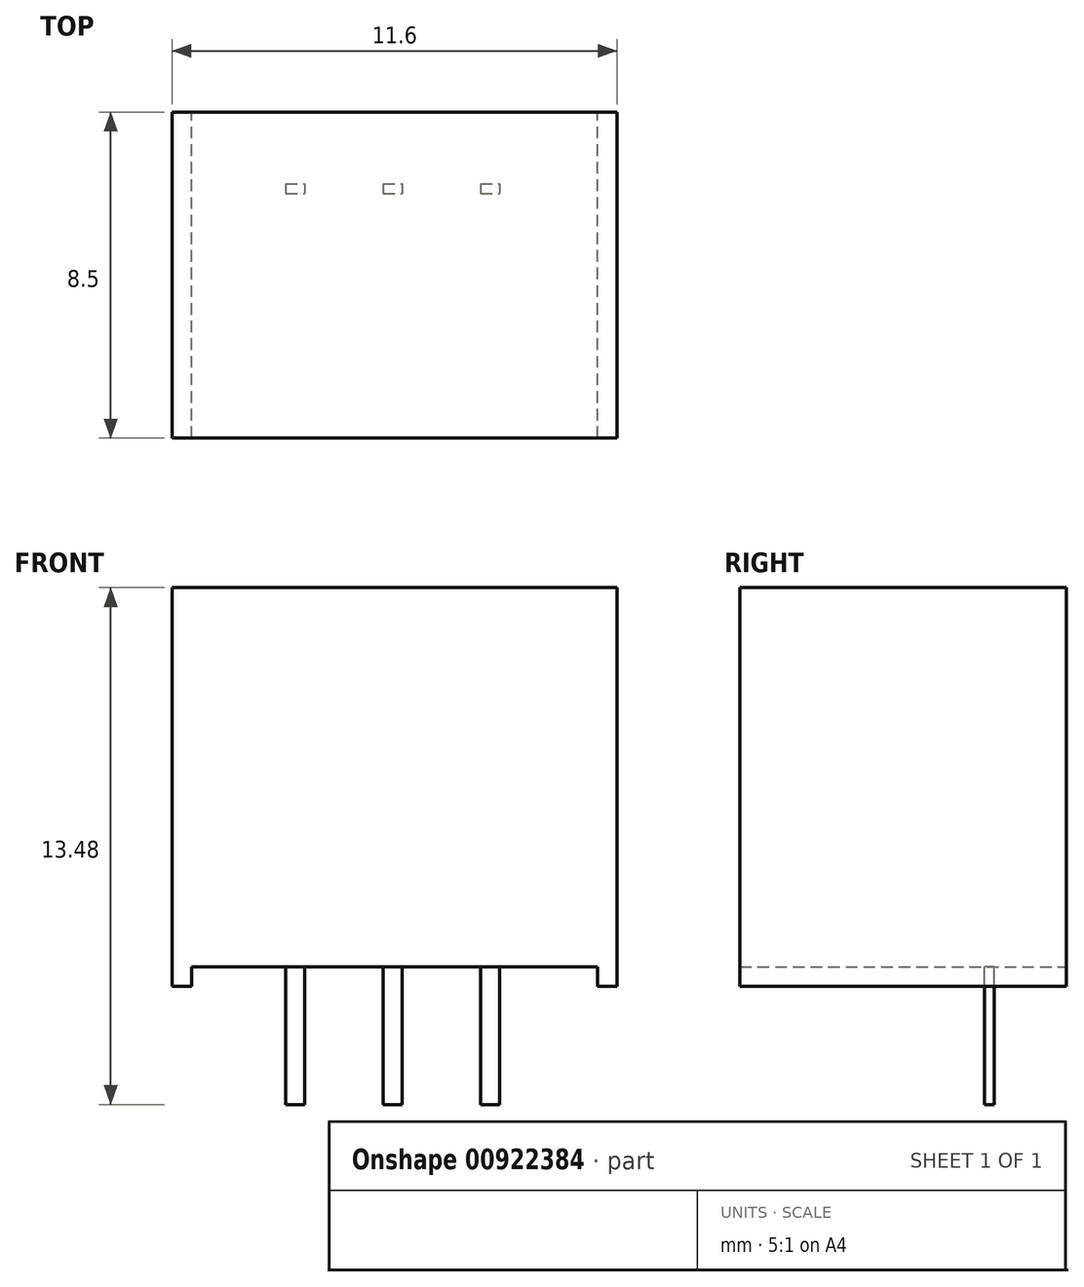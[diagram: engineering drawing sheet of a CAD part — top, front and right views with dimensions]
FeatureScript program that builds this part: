
annotation { "Feature Type Name" : "Feature", "Feature Type Description" : "" }
export const myFeature = defineFeature(function(context is Context, id is Id, definition is map)
    precondition{}
    {
        {
            var Q0;
            Q0=qCreatedBy(makeId("Front.planeOp"),FACE);
            var sketch = newSketch(context, id + "F0", { "sketchPlane" : qUnion([Q0])});
            skLineSegment(sketch, "E0.bottom", {"start": v(-5.8, 5.2) * mm, "end": v(5.8, 5.2) * mm});
            skLineSegment(sketch, "E0.top", {"start": v(-5.8, -5.2) * mm, "end": v(5.8, -5.2) * mm});
            skLineSegment(sketch, "E0.left", {"start": v(-5.8, 5.2) * mm, "end": v(-5.8, -5.2) * mm});
            skLineSegment(sketch, "E0.right", {"start": v(5.8, 5.2) * mm, "end": v(5.8, -5.2) * mm});
            skPoint(sketch, "E0.middle", {"position": v(0, 0) * mm});
            skLineSegment(sketch, "E1", {"start": v(-5.8, -5.2) * mm, "end": v(-5.29, -5.2) * mm});
            skLineSegment(sketch, "E2", {"start": v(-5.29, -5.2) * mm, "end": v(-5.29, -4.69) * mm});
            skLineSegment(sketch, "E3.MirrorCS", {"start": v(5.8, -5.2) * mm, "end": v(5.29, -5.2) * mm});
            skLineSegment(sketch, "E4.MirrorCS", {"start": v(5.29, -5.2) * mm, "end": v(5.29, -4.69) * mm});
            skLineSegment(sketch, "E5", {"start": v(-5.29, -4.69) * mm, "end": v(5.29, -4.69) * mm});
            skSolve(sketch);
        }
        {
            var Q0;
            Q0=makeQuery(id+"F0.imprint","IMPRINT",FACE,{"disambiguationData":[TD([[makeQuery(id+"F0.imprint","IMPRINT",EDGE,{"derivedFrom":sQuery(id+"F0.wireOp",EDGE,"E0.bottom")}),-1.0]])]});
            extrude(context, id + "F1", {"entities" : qUnion([Q0]), "endBound" : BoundingType.SYMMETRIC, "depth" : 8.5 * mm, "offsetDistance" : 25 * mm});
        }
        {
            var Q0;
            Q0=makeQuery(id+"F1.opExtrude","SWEPT_FACE",FACE,{"disambiguationData":[OSD([sQuery(id+"F0.wireOp",EDGE,"E5")])]});
            var sketch = newSketch(context, id + "F2", { "sketchPlane" : qUnion([Q0])});
            skLineSegment(sketch, "E6", {"start": v(-5.29, 4.25) * mm, "end": v(-2.59, 4.25) * mm});
            skLineSegment(sketch, "E7.bottom", {"start": v(-2.84, 2.37) * mm, "end": v(-2.34, 2.37) * mm});
            skLineSegment(sketch, "E7.top", {"start": v(-2.84, 2.12) * mm, "end": v(-2.34, 2.12) * mm});
            skLineSegment(sketch, "E7.left", {"start": v(-2.84, 2.37) * mm, "end": v(-2.84, 2.12) * mm});
            skLineSegment(sketch, "E7.right", {"start": v(-2.34, 2.37) * mm, "end": v(-2.34, 2.12) * mm});
            skPoint(sketch, "E7.middle", {"position": v(-2.59, 2.25) * mm});
            skLineSegment(sketch, "E8.bottom", {"start": v(-0.3, 2.38) * mm, "end": v(0.2, 2.38) * mm});
            skLineSegment(sketch, "E8.top", {"start": v(-0.3, 2.13) * mm, "end": v(0.2, 2.13) * mm});
            skLineSegment(sketch, "E8.left", {"start": v(-0.3, 2.38) * mm, "end": v(-0.3, 2.13) * mm});
            skLineSegment(sketch, "E8.right", {"start": v(0.2, 2.38) * mm, "end": v(0.2, 2.13) * mm});
            skPoint(sketch, "E8.middle", {"position": v(-0.05, 2.25) * mm});
            skLineSegment(sketch, "E9.bottom", {"start": v(2.24, 2.38) * mm, "end": v(2.74, 2.38) * mm});
            skLineSegment(sketch, "E9.top", {"start": v(2.24, 2.13) * mm, "end": v(2.74, 2.13) * mm});
            skLineSegment(sketch, "E9.left", {"start": v(2.24, 2.38) * mm, "end": v(2.24, 2.13) * mm});
            skLineSegment(sketch, "E9.right", {"start": v(2.74, 2.38) * mm, "end": v(2.74, 2.13) * mm});
            skPoint(sketch, "E9.middle", {"position": v(2.5, 2.25) * mm});
            skSolve(sketch);
        }
        {
            var Q0;
            Q0=makeQuery(id+"F2.imprint","IMPRINT",FACE,{"disambiguationData":[TD([[makeQuery(id+"F2.imprint","IMPRINT",EDGE,{"derivedFrom":sQuery(id+"F2.wireOp",EDGE,"E9.bottom")}),-1.0]])]});
            var Q1;
            Q1=makeQuery(id+"F2.imprint","IMPRINT",FACE,{"disambiguationData":[TD([[makeQuery(id+"F2.imprint","IMPRINT",EDGE,{"derivedFrom":sQuery(id+"F2.wireOp",EDGE,"E8.bottom")}),-1.0]])]});
            var Q2;
            Q2=makeQuery(id+"F2.imprint","IMPRINT",FACE,{"disambiguationData":[TD([[makeQuery(id+"F2.imprint","IMPRINT",EDGE,{"derivedFrom":sQuery(id+"F2.wireOp",EDGE,"E7.bottom")}),-1.0]])]});
            extrude(context, id + "F3", {"entities" : qUnion([Q0, Q1, Q2]), "depth" : (4.1 - 0.51) * mm, "offsetDistance" : 25 * mm});
        }
        {
            var Q0;
            Q0=makeQuery(id+"F1.opExtrude","SWEPT_BODY",BODY,{"disambiguationData":[OSD([sQuery(id+"F0.wireOp",EDGE,"E0.bottom"),sQuery(id+"F0.wireOp",EDGE,"E0.left"),sQuery(id+"F0.wireOp",EDGE,"E0.right"),sQuery(id+"F0.wireOp",EDGE,"E1"),sQuery(id+"F0.wireOp",EDGE,"E2"),sQuery(id+"F0.wireOp",EDGE,"E3.MirrorCS"),sQuery(id+"F0.wireOp",EDGE,"E4.MirrorCS"),sQuery(id+"F0.wireOp",EDGE,"E5")])]});
            var Q1;
            Q1=makeQuery(id+"F3.opExtrude","SWEPT_BODY",BODY,{"disambiguationData":[OSD([sQuery(id+"F2.wireOp",EDGE,"E7.bottom"),sQuery(id+"F2.wireOp",EDGE,"E7.top"),sQuery(id+"F2.wireOp",EDGE,"E7.left"),sQuery(id+"F2.wireOp",EDGE,"E7.right")])]});
            var Q2;
            Q2=makeQuery(id+"F3.opExtrude","SWEPT_BODY",BODY,{"disambiguationData":[OSD([sQuery(id+"F2.wireOp",EDGE,"E8.bottom"),sQuery(id+"F2.wireOp",EDGE,"E8.top"),sQuery(id+"F2.wireOp",EDGE,"E8.left"),sQuery(id+"F2.wireOp",EDGE,"E8.right")])]});
            var Q3;
            Q3=makeQuery(id+"F3.opExtrude","SWEPT_BODY",BODY,{"disambiguationData":[OSD([sQuery(id+"F2.wireOp",EDGE,"E9.bottom"),sQuery(id+"F2.wireOp",EDGE,"E9.top"),sQuery(id+"F2.wireOp",EDGE,"E9.left"),sQuery(id+"F2.wireOp",EDGE,"E9.right")])]});
            transform(context, id + "F4", {"entities" : qUnion([Q0, Q1, Q2, Q3]), "transformType" : TransformType.TRANSLATION_3D, "dx" : 0 * mm, "dy" : 0 * mm, "dz" : 5.2 * mm, "makeCopy" : false});
        }
        {
            var Q0;
            Q0=makeQuery(id+"F3.opExtrude","SWEPT_BODY",BODY,{"disambiguationData":[OSD([sQuery(id+"F2.wireOp",EDGE,"E7.bottom"),sQuery(id+"F2.wireOp",EDGE,"E7.top"),sQuery(id+"F2.wireOp",EDGE,"E7.left"),sQuery(id+"F2.wireOp",EDGE,"E7.right")])]});
            var Q1;
            Q1=makeQuery(id+"F3.opExtrude","SWEPT_BODY",BODY,{"disambiguationData":[OSD([sQuery(id+"F2.wireOp",EDGE,"E9.bottom"),sQuery(id+"F2.wireOp",EDGE,"E9.top"),sQuery(id+"F2.wireOp",EDGE,"E9.left"),sQuery(id+"F2.wireOp",EDGE,"E9.right")])]});
            var Q2;
            Q2=makeQuery(id+"F3.opExtrude","SWEPT_BODY",BODY,{"disambiguationData":[OSD([sQuery(id+"F2.wireOp",EDGE,"E8.bottom"),sQuery(id+"F2.wireOp",EDGE,"E8.top"),sQuery(id+"F2.wireOp",EDGE,"E8.left"),sQuery(id+"F2.wireOp",EDGE,"E8.right")])]});
            var Q3;
            Q3=qCreatedBy(makeId("Front.planeOp"),FACE);
            mirror(context, id + "F5", {"entities" : qUnion([Q0, Q1, Q2]), "mirrorPlane" : qUnion([Q3])});
        }
        {
            var Q0;
            Q0=makeQuery(id+"F3.opExtrude","SWEPT_BODY",BODY,{"disambiguationData":[OSD([sQuery(id+"F2.wireOp",EDGE,"E7.bottom"),sQuery(id+"F2.wireOp",EDGE,"E7.top"),sQuery(id+"F2.wireOp",EDGE,"E7.left"),sQuery(id+"F2.wireOp",EDGE,"E7.right")])]});
            var Q1;
            Q1=makeQuery(id+"F3.opExtrude","SWEPT_BODY",BODY,{"disambiguationData":[OSD([sQuery(id+"F2.wireOp",EDGE,"E8.bottom"),sQuery(id+"F2.wireOp",EDGE,"E8.top"),sQuery(id+"F2.wireOp",EDGE,"E8.left"),sQuery(id+"F2.wireOp",EDGE,"E8.right")])]});
            var Q2;
            Q2=makeQuery(id+"F3.opExtrude","SWEPT_BODY",BODY,{"disambiguationData":[OSD([sQuery(id+"F2.wireOp",EDGE,"E9.bottom"),sQuery(id+"F2.wireOp",EDGE,"E9.top"),sQuery(id+"F2.wireOp",EDGE,"E9.left"),sQuery(id+"F2.wireOp",EDGE,"E9.right")])]});
            deleteBodies(context, id + "F6", {"entities" : qUnion([Q0, Q1, Q2])});
        }
    });
